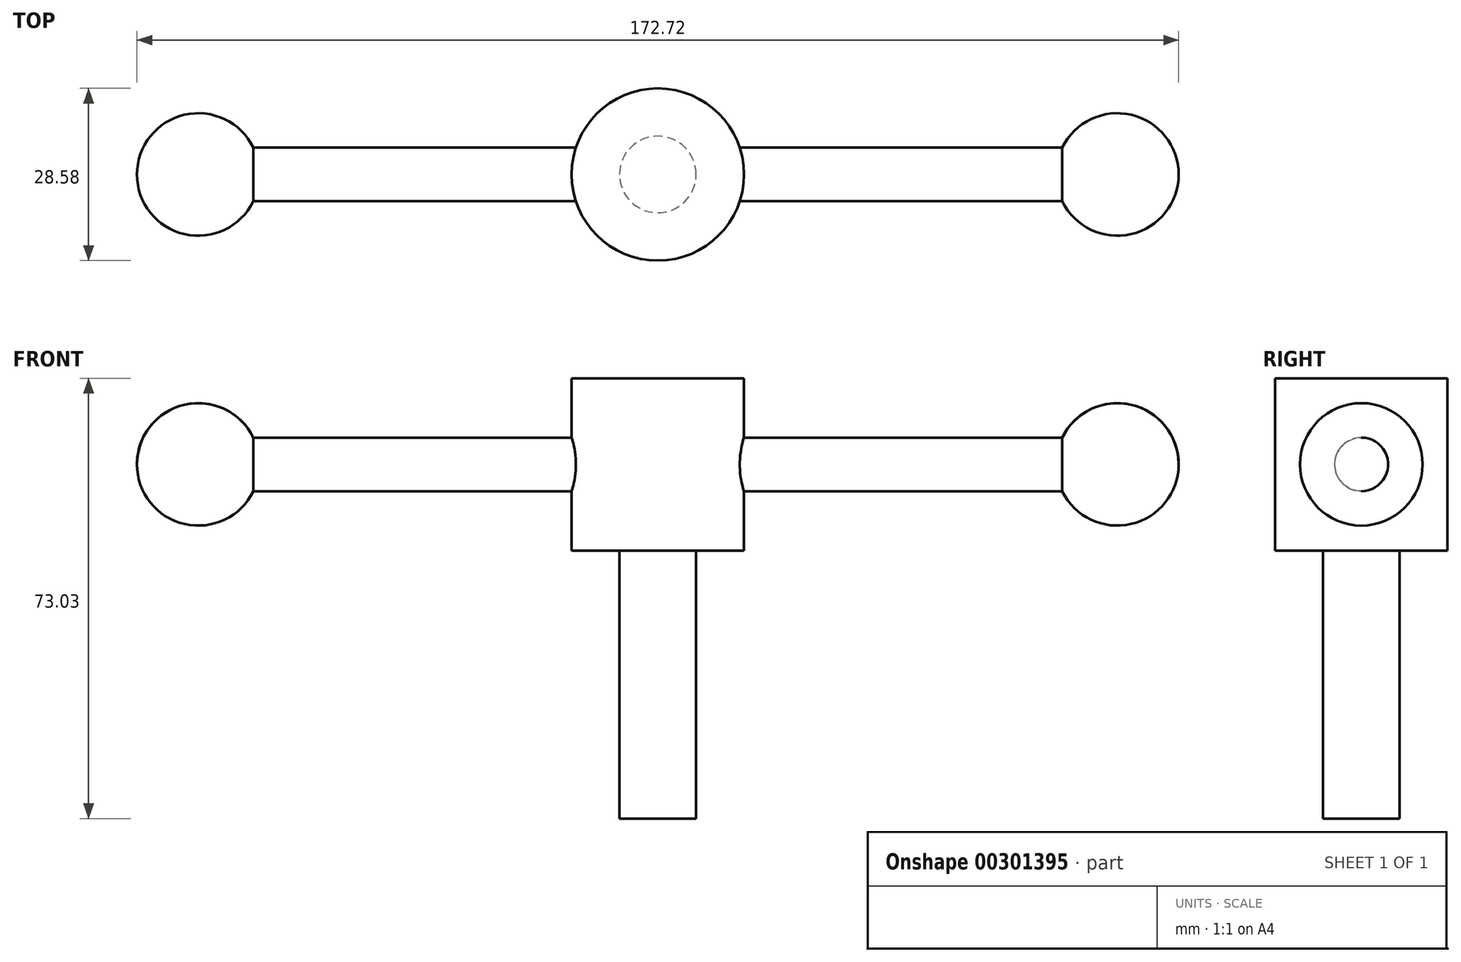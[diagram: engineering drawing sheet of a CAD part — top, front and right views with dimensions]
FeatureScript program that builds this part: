
annotation { "Feature Type Name" : "Feature", "Feature Type Description" : "" }
export const myFeature = defineFeature(function(context is Context, id is Id, definition is map)
    precondition{}
    {
        {
            var Q0;
            Q0=qCreatedBy(makeId("Top.planeOp"),FACE);
            var sketch = newSketch(context, id + "F0", { "sketchPlane" : qUnion([Q0])});
            skCircle(sketch, "E0", {"center": v(0, 0) * mm, "radius": 14.29 * mm});
            skSolve(sketch);
        }
        {
            var Q0;
            Q0=makeQuery(id+"F0.imprint","IMPRINT",FACE,{"disambiguationData":[TD([[makeQuery(id+"F0.imprint","IMPRINT",EDGE,{"derivedFrom":sQuery(id+"F0.wireOp",EDGE,"E0")}),1.0]])]});
            extrude(context, id + "F1", {"entities" : qUnion([Q0]), "endBound" : BoundingType.SYMMETRIC, "depth" : 28.57 * mm});
        }
        {
            var Q0;
            Q0=makeQuery(id+"F1.opExtrude","CAP_FACE",FACE,{"disambiguationData":[OSD([sQuery(id+"F0.wireOp",EDGE,"E0")])],"isStart":true});
            var sketch = newSketch(context, id + "F2", { "sketchPlane" : qUnion([Q0])});
            skCircle(sketch, "E1", {"center": v(0, 0) * mm, "radius": 6.35 * mm});
            skSolve(sketch);
        }
        {
            var Q0;
            Q0=makeQuery(id+"F2.imprint","IMPRINT",FACE,{"disambiguationData":[TD([[makeQuery(id+"F2.imprint","IMPRINT",EDGE,{"derivedFrom":sQuery(id+"F2.wireOp",EDGE,"E1")}),1.0]])]});
            extrude(context, id + "F3", {"entities" : qUnion([Q0]), "operationType" : NewBodyOperationType.ADD, "depth" : 44.45 * mm});
        }
        {
            var Q0;
            Q0=qCreatedBy(makeId("Right.planeOp"),FACE);
            var sketch = newSketch(context, id + "F4", { "sketchPlane" : qUnion([Q0])});
            skCircle(sketch, "E2", {"center": v(0, 0) * mm, "radius": 4.45 * mm});
            skSolve(sketch);
        }
        {
            var Q0;
            Q0 = qSketchRegion(id + "F4", true);
            extrude(context, id + "F5", {"entities" : qUnion([Q0]), "operationType" : NewBodyOperationType.ADD, "endBound" : BoundingType.SYMMETRIC, "depth" : 152.4 * mm});
        }
        {
            var Q0;
            Q0=qCreatedBy(makeId("Front.planeOp"),FACE);
            var sketch = newSketch(context, id + "F6", { "sketchPlane" : qUnion([Q0])});
            skArc(sketch, "E3", {"start": v(-66.04, 0) * mm, "mid": v(-76.2, 10.16) * mm, "end": v(-86.36, 0) * mm});
            skLineSegment(sketch, "E4", {"start": v(-86.36, 0) * mm, "end": v(-66.04, 0) * mm});
            skSolve(sketch);
        }
        {
            var Q0;
            Q0=makeQuery(id+"F6.imprint","IMPRINT",FACE,{"disambiguationData":[TD([[makeQuery(id+"F6.imprint","IMPRINT",EDGE,{"derivedFrom":sQuery(id+"F6.wireOp",EDGE,"E3")}),1.0]])]});
            var Q1;
            Q1=makeQuery(id+"F5.opExtrude","CAP_EDGE",EDGE,{"disambiguationData":[OSD([sQuery(id+"F4.wireOp",EDGE,"E2")])],"isStart":true});
            revolve(context, id + "F7", {"operationType" : NewBodyOperationType.ADD, "entities" : qUnion([Q0]), "axis" : qUnion([Q1]), "revolveType" : RevolveType.FULL});
        }
        {
            var Q0;
            Q0=qCreatedBy(makeId("Front.planeOp"),FACE);
            var sketch = newSketch(context, id + "F8", { "sketchPlane" : qUnion([Q0])});
            skArc(sketch, "E5", {"start": v(86.36, 0) * mm, "mid": v(76.2, 10.16) * mm, "end": v(66.04, 0) * mm});
            skLineSegment(sketch, "E6", {"start": v(86.36, 0) * mm, "end": v(66.04, 0) * mm});
            skSolve(sketch);
        }
        {
            var Q0;
            Q0=makeQuery(id+"F8.imprint","IMPRINT",FACE,{"disambiguationData":[TD([[makeQuery(id+"F8.imprint","IMPRINT",EDGE,{"derivedFrom":sQuery(id+"F8.wireOp",EDGE,"E5")}),1.0]])]});
            var Q1;
            Q1=makeQuery(id+"F5.opExtrude","CAP_EDGE",EDGE,{"disambiguationData":[OSD([sQuery(id+"F4.wireOp",EDGE,"E2")])],"isStart":false});
            revolve(context, id + "F9", {"operationType" : NewBodyOperationType.ADD, "entities" : qUnion([Q0]), "axis" : qUnion([Q1]), "revolveType" : RevolveType.FULL});
        }
    });
